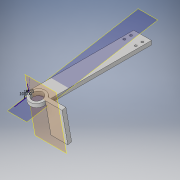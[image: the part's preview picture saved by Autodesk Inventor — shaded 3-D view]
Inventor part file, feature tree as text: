
AUTODESK INVENTOR PART (.ipt)
format: ipt  version: 2017 (Build 210142000, 142)  size: 178,688 bytes
history: native  units: in
note: dims shown in document units (in); Inventor stores cm internally (conversion verified against a paired STEP export)
features: sketch x6, projected_geometry x6, extrude x3, plane x2, hole x2
ambient origin geometry x8: Origin, YZ Plane, XZ Plane, XY Plane, X Axis, Y Axis, Z Axis, Center Point
bodies: Solid1 (feature_tree)
feature tree (19):
  extrude  "Extrusion1"  Depth=5.0in
  sketch  "Sketch2"  dims[d2=0.1875in d3=0.0in d4=0.6871in]
  plane  "Work Plane1"
  extrude  "Extrusion2"  Depth=0.1875in
  hole  "Hole2"  [1 undecoded]
  plane  "Work Plane3"
  hole  "Hole3"  [1 undecoded]
  extrude  "Extrusion4"  Depth=0.375in
  sketch  "Sketch1"  dims[d0=0.85in d1=5.0in]
  sketch  "Sketch3"  dims[d5=0.75in d6=0.85in]
  projected_geometry  "Projected Loop1"
  projected_geometry  "Projected Loop2"
  sketch  "Sketch5"  dims[d7=0.425in d8=0.1875in d9=0.0in]
  projected_geometry  "Projected Loop4"
  sketch  "Sketch9"  dims[d17=0.51in d18=0.75in d19=0.375in d20=0.25in d21=0.5635in d22=1.0in d23=0.8108in d24=0.0687in]
  projected_geometry  "Projected Loop10"
  sketch  "Sketch10"  dims[d25=90.0deg d34=0.6299in d35=0.315in d36=0.1575in d37=0.85in d38=0.425in d39=0.44in d40=0.11in d41=0.75in d42=0.375in d43=0.25in d44=0.5635in d45=1.0in d46=0.8108in d47=0.875in d50=0.8033in d51=0.1875in d52=0.0in d53=0.1875in d54=1.59in]
  projected_geometry  "Projected Loop11"
  projected_geometry  "Projected Loop12"
note: 2 required parameter values undecoded (feature->parameter linkage not recoverable at this tier; creation-order binding heuristic only, values carry confidence <= 0.55)
